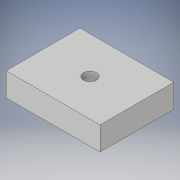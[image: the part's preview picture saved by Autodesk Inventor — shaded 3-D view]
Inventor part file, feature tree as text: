
AUTODESK INVENTOR PART (.ipt)
format: ipt  version: 2019 (Build 230136000, 136)  size: 101,376 bytes
history: native  units: in
note: dims shown in document units (in); Inventor stores cm internally (conversion verified against a paired STEP export)
features: sketch x2, extrude x1, hole x1, projected_geometry x1
ambient origin geometry x8: Origin, YZ Plane, XZ Plane, XY Plane, X Axis, Y Axis, Z Axis, Center Point
bodies: Solid1 (feature_tree)
feature tree (5):
  extrude  "Extrusion1"  Depth=0.787in
  hole  "Hole1"  [1 undecoded]
  sketch  "Sketch1"  dims[d0=1.0in d1=0.787in]
  sketch  "Sketch2"  dims[d2=0.25in d3=0.0in d4=0.787in d5=1.0in d6=0.5in d7=0.3935in d8=0.138in d9=0.75in d10=0.375in d11=0.25in d12=0.5635in d13=1.0in d14=0.8108in]
  projected_geometry  "Projected Loop1"
note: 1 required parameter value undecoded (feature->parameter linkage not recoverable at this tier; creation-order binding heuristic only, values carry confidence <= 0.55)
